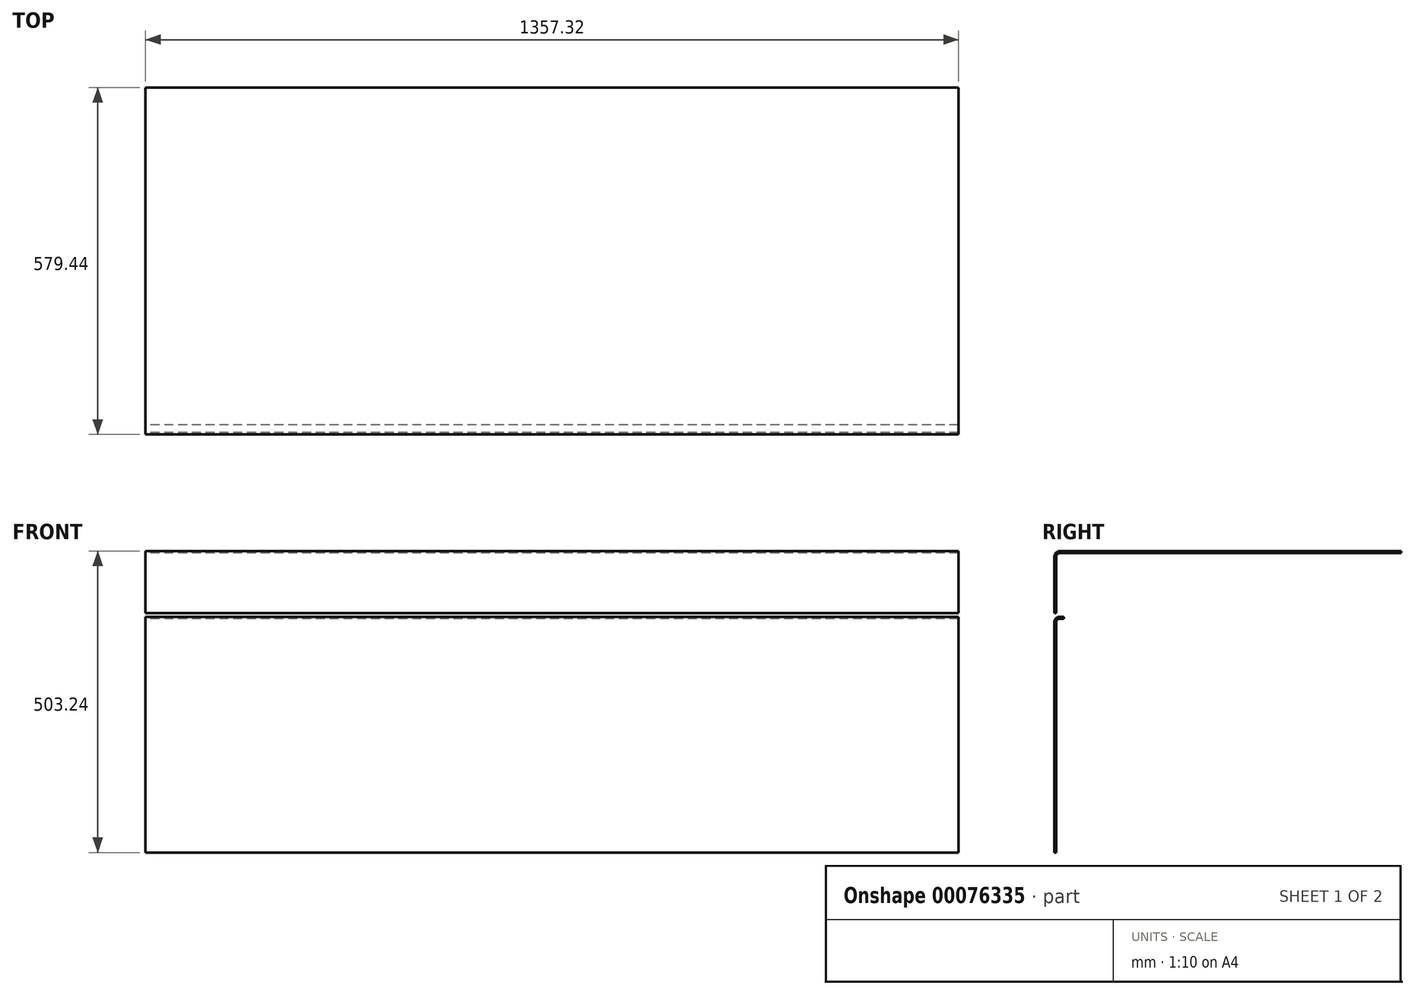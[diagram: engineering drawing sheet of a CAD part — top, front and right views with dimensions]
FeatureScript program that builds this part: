
annotation { "Feature Type Name" : "Feature", "Feature Type Description" : "" }
export const myFeature = defineFeature(function(context is Context, id is Id, definition is map)
    precondition{}
    {
        {
            var Q0;
            Q0=qCreatedBy(makeId("Right.planeOp"),FACE);
            var sketch = newSketch(context, id + "F0", { "sketchPlane" : qUnion([Q0])});
            skLineSegment(sketch, "E0", {"start": v(579.44, 0) * mm, "end": v(9.53, 0) * mm});
            skArc(sketch, "E1", {"start": v(9.53, 0) * mm, "mid": v(2.79, -2.79) * mm, "end": v(0, -9.53) * mm});
            skLineSegment(sketch, "E2", {"start": v(0, -9.53) * mm, "end": v(0, -103.19) * mm});
            skLineSegment(sketch, "E3", {"start": v(0, -103.19) * mm, "end": v(3.18, -103.19) * mm});
            skLineSegment(sketch, "E4", {"start": v(3.18, -103.19) * mm, "end": v(3.18, -9.53) * mm});
            skLineSegment(sketch, "E5", {"start": v(579.44, 0) * mm, "end": v(579.44, -3.17) * mm});
            skLineSegment(sketch, "E6", {"start": v(579.44, -3.17) * mm, "end": v(9.53, -3.17) * mm});
            skArc(sketch, "E7", {"start": v(9.53, -3.18) * mm, "mid": v(5.03, -5.03) * mm, "end": v(3.18, -9.53) * mm});
            skLineSegment(sketch, "E8", {"start": v(579.44, -22.22) * mm, "end": v(17.46, -22.22) * mm, "construction": true});
            skLineSegment(sketch, "E9", {"start": v(17.46, -22.22) * mm, "end": v(17.46, -120.65) * mm, "construction": true});
            skLineSegment(sketch, "E10", {"start": v(17.46, -120.65) * mm, "end": v(3.17, -120.65) * mm, "construction": true});
            skLineSegment(sketch, "E11", {"start": v(3.18, -120.65) * mm, "end": v(3.18, -503.24) * mm, "construction": true});
            skLineSegment(sketch, "E12", {"start": v(3.17, -503.24) * mm, "end": v(579.44, -503.24) * mm, "construction": true});
            skLineSegment(sketch, "E13", {"start": v(579.44, -503.24) * mm, "end": v(579.44, -22.22) * mm, "construction": true});
            skLineSegment(sketch, "E14.bottom", {"start": v(576.26, 609.6) * mm, "end": v(579.44, 609.6) * mm, "construction": true});
            skLineSegment(sketch, "E14.top", {"start": v(576.26, 0) * mm, "end": v(579.44, 0) * mm, "construction": true});
            skLineSegment(sketch, "E14.left", {"start": v(576.26, 609.6) * mm, "end": v(576.26, 0) * mm, "construction": true});
            skLineSegment(sketch, "E14.right", {"start": v(579.44, 609.6) * mm, "end": v(579.44, 0) * mm, "construction": true});
            skLineSegment(sketch, "E15", {"start": v(3.17, -503.24) * mm, "end": v(0, -503.24) * mm});
            skLineSegment(sketch, "E16", {"start": v(0, -503.24) * mm, "end": v(0, -119.06) * mm});
            skLineSegment(sketch, "E17", {"start": v(9.53, -109.54) * mm, "end": v(15.87, -109.54) * mm});
            skLineSegment(sketch, "E18", {"start": v(15.88, -109.54) * mm, "end": v(15.88, -112.71) * mm});
            skLineSegment(sketch, "E19", {"start": v(15.87, -112.71) * mm, "end": v(9.53, -112.71) * mm});
            skLineSegment(sketch, "E20", {"start": v(3.18, -119.06) * mm, "end": v(3.18, -503.24) * mm});
            skArc(sketch, "E21", {"start": v(9.53, -112.71) * mm, "mid": v(5.03, -114.57) * mm, "end": v(3.18, -119.06) * mm});
            skArc(sketch, "E22", {"start": v(9.53, -109.54) * mm, "mid": v(2.79, -112.33) * mm, "end": v(0, -119.06) * mm});
            skSolve(sketch);
        }
        {
            var Q0;
            Q0 = qSketchRegion(id + "F0", true);
            extrude(context, id + "F1", {"entities" : qUnion([Q0]), "endBound" : BoundingType.SYMMETRIC, "depth" : 1357.3 * mm});
        }
    });
